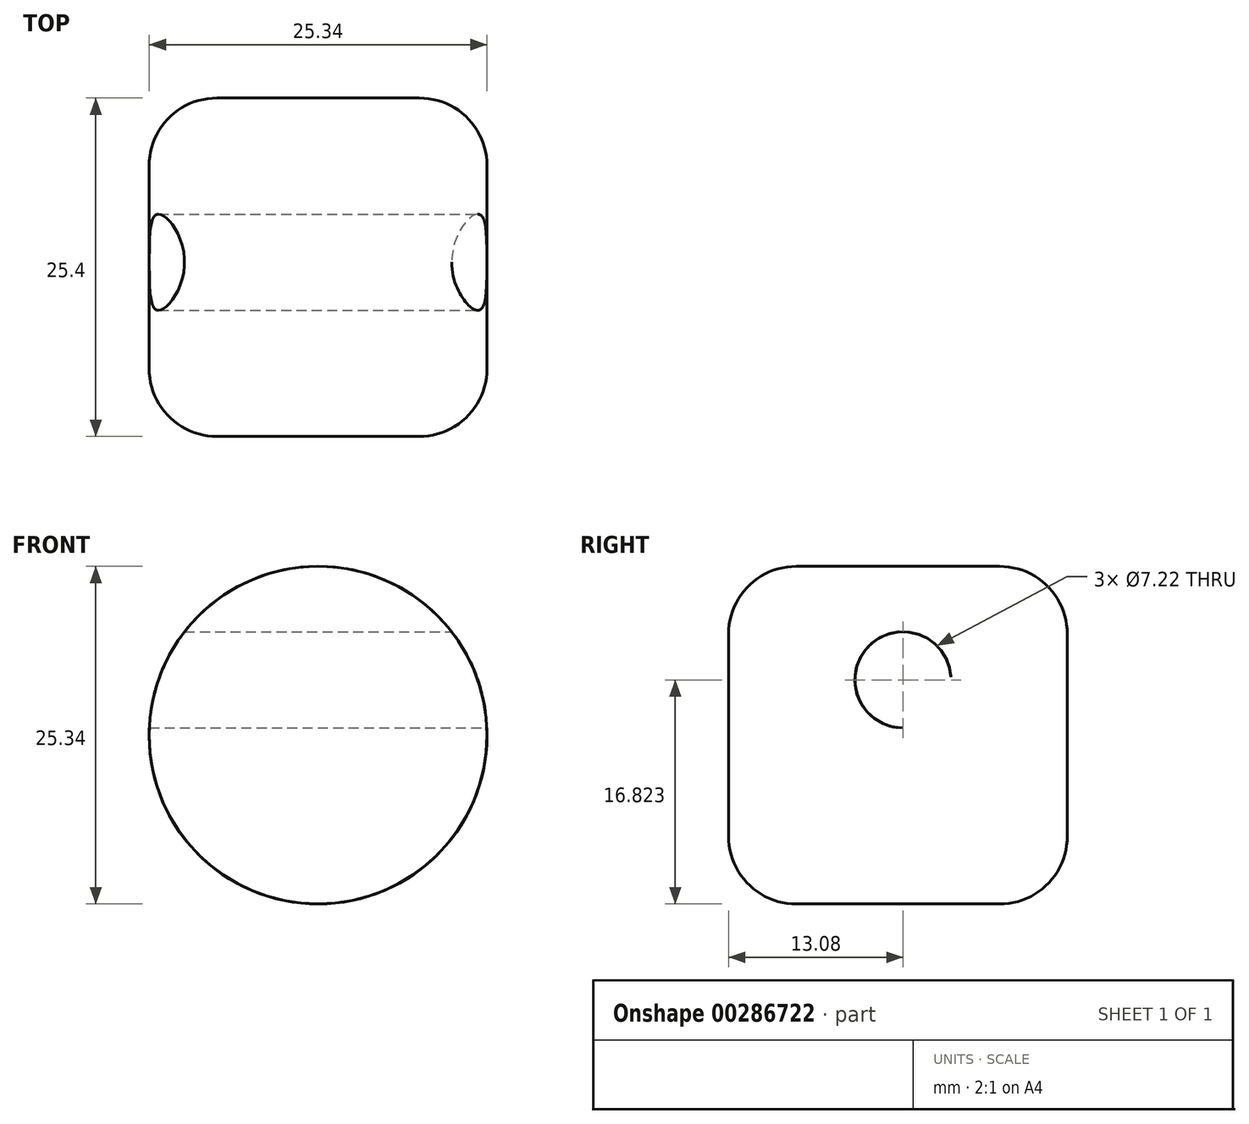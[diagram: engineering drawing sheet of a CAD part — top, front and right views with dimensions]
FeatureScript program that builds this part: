
annotation { "Feature Type Name" : "Feature", "Feature Type Description" : "" }
export const myFeature = defineFeature(function(context is Context, id is Id, definition is map)
    precondition{}
    {
        {
            var Q0;
            Q0=qCreatedBy(makeId("Front.planeOp"),FACE);
            var sketch = newSketch(context, id + "F0", { "sketchPlane" : qUnion([Q0])});
            skCircle(sketch, "E0", {"center": v(0, 0) * mm, "radius": 12.67 * mm});
            skSolve(sketch);
        }
        {
            var Q0;
            Q0=qSketchRegion(id+"F0",true);
            extrude(context, id + "F1", {"entities" : qUnion([Q0]), "depth" : 25.4 * mm});
        }
        {
            var Q0;
            Q0=makeQuery(id+"F1.opExtrude","CAP_EDGE",EDGE,{"disambiguationData":[OSD([sQuery(id+"F0.wireOp",EDGE,"E0")])],"isStart":false});
            fillet(context, id + "F2", {"entities" : qUnion([Q0]), "radius" : 5.08 * mm, "tangentPropagation" : true, "allowEdgeOverflow" : false});
        }
        {
            var Q0;
            Q0=makeQuery(id+"F1.opExtrude","CAP_EDGE",EDGE,{"disambiguationData":[OSD([sQuery(id+"F0.wireOp",EDGE,"E0")])],"isStart":true});
            fillet(context, id + "F3", {"entities" : qUnion([Q0]), "radius" : 5.08 * mm, "tangentPropagation" : true, "allowEdgeOverflow" : false});
        }
        {
            var Q0;
            Q0=qCreatedBy(makeId("Right.planeOp"),FACE);
            var sketch = newSketch(context, id + "F4", { "sketchPlane" : qUnion([Q0])});
            skCircle(sketch, "E1", {"center": v(-12.32, 4.15) * mm, "radius": 3.6 * mm});
            skSolve(sketch);
        }
        {
            var Q0;
            Q0=qSketchRegion(id+"F4",true);
            extrude(context, id + "F5", {"entities" : qUnion([Q0]), "operationType" : NewBodyOperationType.REMOVE, "oppositeDirection" : true, "depth" : 50.8 * mm});
        }
        {
            var Q0;
            Q0=makeQuery(id+"F5.boolean.opBoolean","COPY",FACE,{"derivedFrom":makeQuery(id+"F5.opExtrude","CAP_FACE",FACE,{"disambiguationData":[OSD([sQuery(id+"F4.wireOp",EDGE,"E1")])],"isStart":true})});
            extrude(context, id + "F6", {"entities" : qUnion([Q0]), "operationType" : NewBodyOperationType.REMOVE, "oppositeDirection" : true, "depth" : 101.6 * mm});
        }
    });
